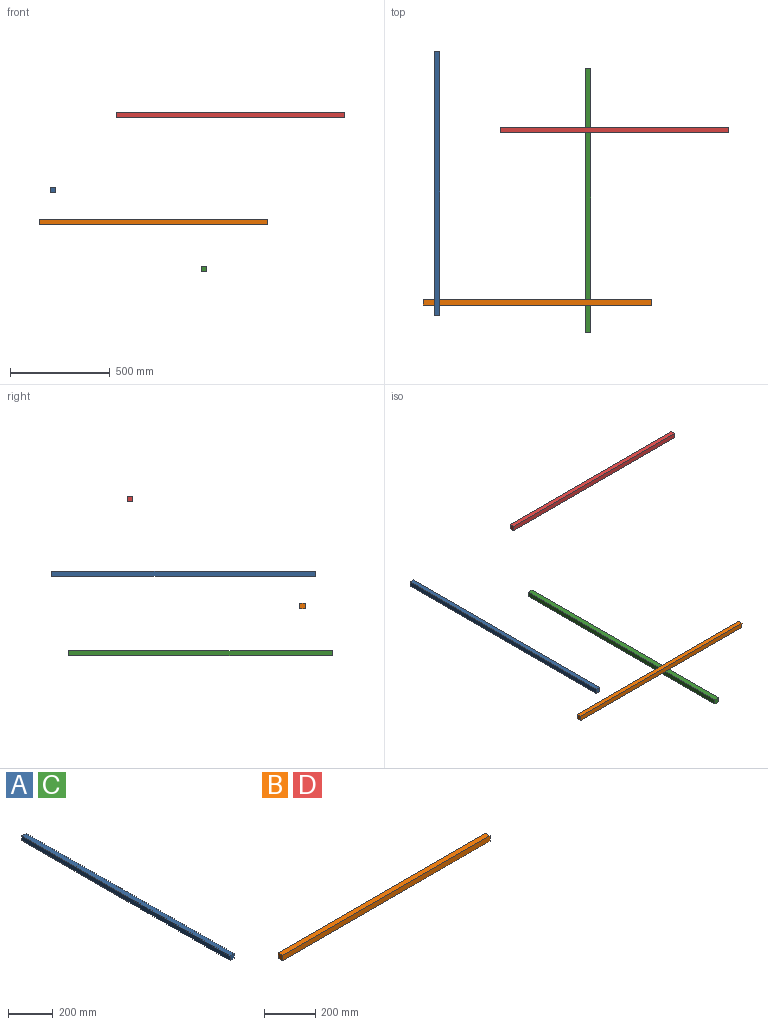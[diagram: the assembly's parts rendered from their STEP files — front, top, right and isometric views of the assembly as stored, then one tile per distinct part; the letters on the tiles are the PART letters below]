
ASSEMBLY  parts=4 mates=1
PART A: 6 faces, bbox 25.4x1320.8x25.4 mm
  f0: plane 1320.8x25.4mm, normal (0,0,1), area 33548.3mm2, adj f1,f3,f4,f5
  f1: plane 1320.8x25.4mm, normal (-1,0,0), area 33548.3mm2, adj f0,f2,f4,f5
  f2: plane 1320.8x25.4mm, normal (0,0,-1), area 33548.3mm2, adj f1,f3,f4,f5
  f3: plane 1320.8x25.4mm, normal (1,0,0), area 33548.3mm2, adj f0,f2,f4,f5
  f4: plane 25.4x25.4mm, normal (0,-1,0), area 645.2mm2, adj f0,f1,f2,f3
  f5: plane 25.4x25.4mm, normal (0,1,0), area 645.2mm2, adj f0,f1,f2,f3
PART B: 6 faces, bbox 1143x25.4x25.4 mm
  f0: plane 1143x25.4mm, normal (0,0,1), area 29032.2mm2, adj f1,f3,f4,f5
  f1: plane 1143x25.4mm, normal (0,-1,0), area 29032.2mm2, adj f0,f2,f4,f5
  f2: plane 1143x25.4mm, normal (0,0,-1), area 29032.2mm2, adj f1,f3,f4,f5
  f3: plane 1143x25.4mm, normal (0,1,0), area 29032.2mm2, adj f0,f2,f4,f5
  f4: plane 25.4x25.4mm, normal (1,0,0), area 645.2mm2, adj f0,f1,f2,f3
  f5: plane 25.4x25.4mm, normal (-1,0,0), area 645.2mm2, adj f0,f1,f2,f3
PART C: same geometry as A
PART D: same geometry as B
PLACE A t=(-1154.83,406.73,-127.55)mm
PLACE B rot(axis=(0,1,0),0deg) t=(-1273.88,-804.18,-282.25)mm
PLACE C t=(-399.65,322.11,-525.97)mm
PLACE D t=(-883.93,61.52,255.36)mm
MATE parallel C.f4 <-> B.f3  axis (0,-1,0) through (-446.96,-998.69,-479.95)mm
